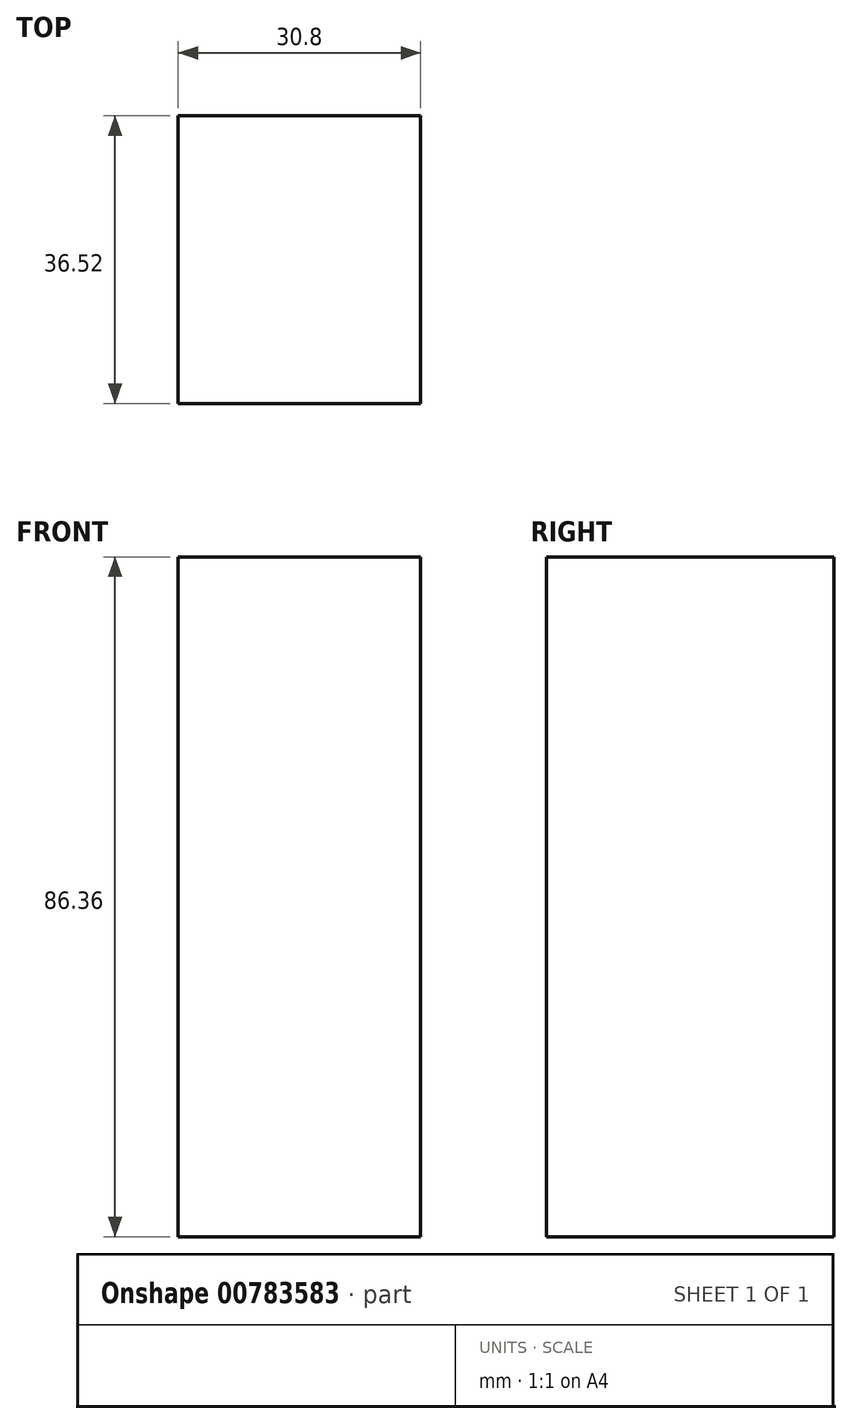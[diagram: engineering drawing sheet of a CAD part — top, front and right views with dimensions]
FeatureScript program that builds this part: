
annotation { "Feature Type Name" : "Feature", "Feature Type Description" : "" }
export const myFeature = defineFeature(function(context is Context, id is Id, definition is map)
    precondition{}
    {
        {
            var Q0;
            Q0=qCreatedBy(makeId("Top.planeOp"),FACE);
            var sketch = newSketch(context, id + "F0", { "sketchPlane" : qUnion([Q0])});
            skLineSegment(sketch, "E0.bottom", {"start": v(-19.52, 13.37) * mm, "end": v(11.28, 13.37) * mm});
            skLineSegment(sketch, "E0.top", {"start": v(-19.52, -23.15) * mm, "end": v(11.28, -23.15) * mm});
            skLineSegment(sketch, "E0.left", {"start": v(-19.52, 13.37) * mm, "end": v(-19.52, -23.15) * mm});
            skLineSegment(sketch, "E0.right", {"start": v(11.28, 13.37) * mm, "end": v(11.28, -23.15) * mm});
            skPoint(sketch, "E0.middle", {"position": v(-4.12, -4.89) * mm});
            skSolve(sketch);
        }
        {
            var Q0;
            Q0=makeQuery(id+"F0.imprint","IMPRINT",FACE,{"disambiguationData":[TD([[makeQuery(id+"F0.imprint","IMPRINT",EDGE,{"derivedFrom":sQuery(id+"F0.wireOp",EDGE,"E0.bottom")}),-1.0]])]});
            extrude(context, id + "F1", {"entities" : qUnion([Q0]), "depth" : 86.36 * mm, "offsetDistance" : 25.4 * mm});
        }
    });
